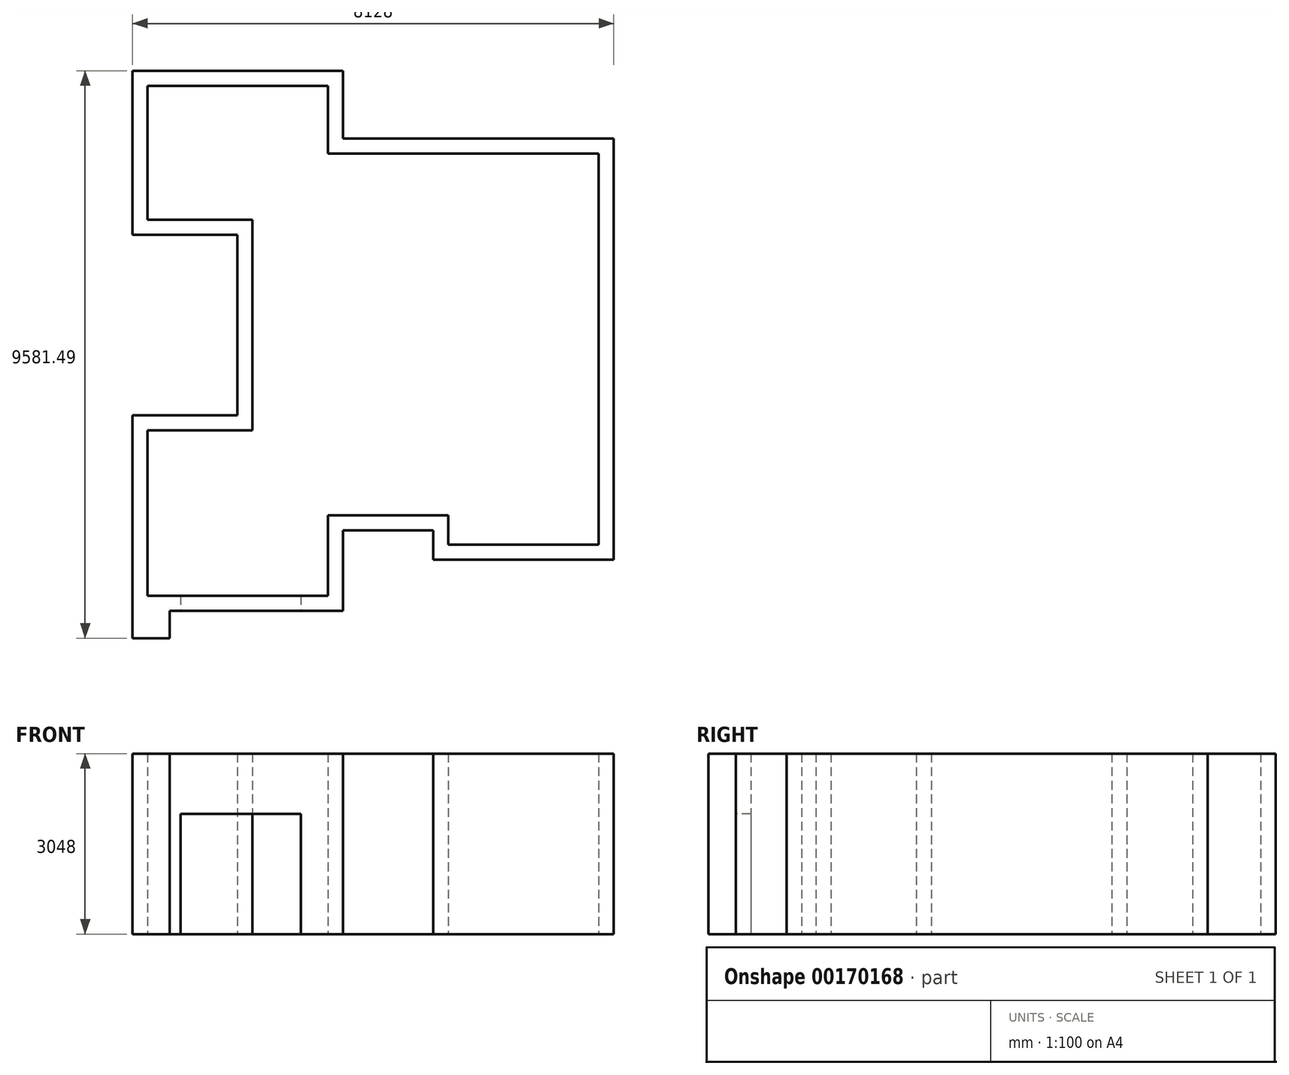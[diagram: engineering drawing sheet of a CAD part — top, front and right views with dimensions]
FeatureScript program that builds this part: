
annotation { "Feature Type Name" : "Feature", "Feature Type Description" : "" }
export const myFeature = defineFeature(function(context is Context, id is Id, definition is map)
    precondition{}
    {
        {
            var Q0;
            Q0=qCreatedBy(makeId("Top.planeOp"),FACE);
            var sketch = newSketch(context, id + "F0", { "sketchPlane" : qUnion([Q0])});
            skLineSegment(sketch, "E0", {"start": v(0, 0) * mm, "end": v(0, -3302) * mm});
            skLineSegment(sketch, "E1", {"start": v(0, -3302) * mm, "end": v(3556, -3302) * mm});
            skLineSegment(sketch, "E2", {"start": v(3556, -3302) * mm, "end": v(3556, -1946.28) * mm});
            skLineSegment(sketch, "E3", {"start": v(3556, -1946.28) * mm, "end": v(5080, -1946.28) * mm});
            skLineSegment(sketch, "E4", {"start": v(5080, -1946.28) * mm, "end": v(5080, -2440.72) * mm});
            skLineSegment(sketch, "E5", {"start": v(5080, -2440.72) * mm, "end": v(8128, -2440.72) * mm});
            skLineSegment(sketch, "E6", {"start": v(8128, -2440.72) * mm, "end": v(8128, 4671.28) * mm});
            skLineSegment(sketch, "E7", {"start": v(8128, 4671.28) * mm, "end": v(3556, 4671.28) * mm});
            skLineSegment(sketch, "E8", {"start": v(3556, 4671.28) * mm, "end": v(3556, 5818.5) * mm});
            skLineSegment(sketch, "E9", {"start": v(3556, 5818.5) * mm, "end": v(0, 5818.5) * mm});
            skLineSegment(sketch, "E10", {"start": v(0, 5818.5) * mm, "end": v(0, 3048) * mm});
            skLineSegment(sketch, "E11", {"start": v(0, 3048) * mm, "end": v(1768.6, 3048) * mm});
            skLineSegment(sketch, "E12", {"start": v(1768.6, 3048) * mm, "end": v(1768.6, 0) * mm});
            skLineSegment(sketch, "E13", {"start": v(1768.6, 0) * mm, "end": v(0, 0) * mm});
            skLineSegment(sketch, "E14.0", {"start": v(3302, 4417.28) * mm, "end": v(3302, 5564.5) * mm});
            skLineSegment(sketch, "E14.1", {"start": v(7874, 4417.28) * mm, "end": v(3302, 4417.28) * mm});
            skLineSegment(sketch, "E14.2", {"start": v(7874, -2186.72) * mm, "end": v(7874, 4417.28) * mm});
            skLineSegment(sketch, "E14.3", {"start": v(2022.6, -254) * mm, "end": v(254, -254) * mm});
            skLineSegment(sketch, "E14.4", {"start": v(2022.6, 3302) * mm, "end": v(2022.6, -254) * mm});
            skLineSegment(sketch, "E14.5", {"start": v(254, 3302) * mm, "end": v(2022.6, 3302) * mm});
            skLineSegment(sketch, "E14.6", {"start": v(254, 5564.5) * mm, "end": v(254, 3302) * mm});
            skLineSegment(sketch, "E14.7", {"start": v(254, -254) * mm, "end": v(254, -3048) * mm});
            skLineSegment(sketch, "E14.8", {"start": v(254, -3048) * mm, "end": v(3302, -3048) * mm});
            skLineSegment(sketch, "E14.9", {"start": v(3302, -3048) * mm, "end": v(3302, -1692.28) * mm});
            skLineSegment(sketch, "E14.10", {"start": v(3302, 5564.5) * mm, "end": v(254, 5564.5) * mm});
            skLineSegment(sketch, "E14.11", {"start": v(3302, -1692.28) * mm, "end": v(5334, -1692.28) * mm});
            skLineSegment(sketch, "E14.12", {"start": v(5334, -1692.28) * mm, "end": v(5334, -2186.72) * mm});
            skLineSegment(sketch, "E14.13", {"start": v(5334, -2186.72) * mm, "end": v(7874, -2186.72) * mm});
            skLineSegment(sketch, "E15", {"start": v(0, -3302) * mm, "end": v(0, -3763) * mm});
            skLineSegment(sketch, "E16", {"start": v(0, -3763) * mm, "end": v(625.36, -3763) * mm});
            skLineSegment(sketch, "E17", {"start": v(625.36, -3763) * mm, "end": v(625.36, -3302) * mm});
            skSolve(sketch);
        }
        {
            var Q0;
            Q0 = qSketchRegion(id + "F0", true);
            extrude(context, id + "F1", {"entities" : qUnion([Q0]), "depth" : 3048 * mm});
        }
        {
            var Q0;
            Q0=makeQuery(id+"F1.opExtrude","SWEPT_FACE",FACE,{"disambiguationData":[OSD([sQuery(id+"F0.wireOp",EDGE,"E1")])]});
            var sketch = newSketch(context, id + "F2", { "sketchPlane" : qUnion([Q0])});
            skLineSegment(sketch, "E18.bottom", {"start": v(812.8, 0) * mm, "end": v(2844.8, 0) * mm});
            skLineSegment(sketch, "E18.top", {"start": v(812.8, 2032) * mm, "end": v(2844.8, 2032) * mm});
            skLineSegment(sketch, "E18.left", {"start": v(812.8, 0) * mm, "end": v(812.8, 2032) * mm});
            skLineSegment(sketch, "E18.right", {"start": v(2844.8, 0) * mm, "end": v(2844.8, 2032) * mm});
            skSolve(sketch);
        }
        {
            var Q0;
            Q0 = qSketchRegion(id + "F2", true);
            extrude(context, id + "F3", {"entities" : qUnion([Q0]), "operationType" : NewBodyOperationType.REMOVE, "oppositeDirection" : true, "depth" : 355.6 * mm});
        }
    });
